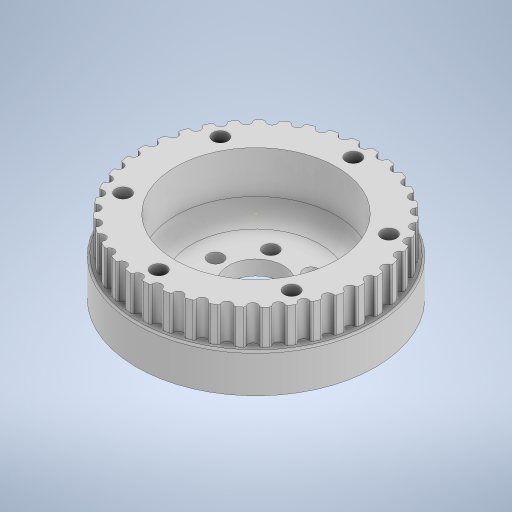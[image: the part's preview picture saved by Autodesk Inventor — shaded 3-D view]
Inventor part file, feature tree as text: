
AUTODESK INVENTOR PART (.ipt)
format: ipt  version: 2024 (Build 280153000, 153)  size: 675,328 bytes
history: native  units: mm
features: sketch x11, extrude x10, projected_geometry x4, fillet x3, pattern_circular x1
ambient origin geometry x8: Origin, YZ Plane, XZ Plane, XY Plane, X Axis, Y Axis, Z Axis, Center Point
bodies: Solid1 (feature_tree)
feature tree (29):
  extrude  "Extrusion1"  Depth=106.0mm
  extrude  "Extrusion2"  Depth=8.0mm TaperAngle=0.0deg
  extrude  "Extrusion3"  Depth=8.0mm TaperAngle=0.0deg
  extrude  "Extrusion4"  Depth=8.1mm
  extrude  "Extrusion5"  Depth=60.0mm
  extrude  "Extrusion6"  Depth=20.0mm TaperAngle=0.0deg
  extrude  "Extrusion7"  Depth=93.5mm
  extrude  "Extrusion8"  Depth=22.0mm TaperAngle=0.0deg
  extrude  "Extrusion9"  Depth=32.0mm TaperAngle=0.0deg
  pattern_circular  "Circular Pattern1"  Count=39 Angle=360.0deg
  fillet  "Fillet1"  Radius=9.0mm
  extrude  "Extrusion10"  Depth=1.0mm
  fillet  "Fillet2"  Radius=130.0mm
  sketch  "Sketch11"  dims[d39=5.1mm d40=125.0mm d41=130.0mm d42=21.0mm d43=0.0mm d44=61.9mm d45=1.0mm d46=1.0mm]
  fillet  "Fillet3"  Radius=21.0mm
  sketch  "Sketch1"  dims[d0=125.0mm d1=106.0mm]
  sketch  "Sketch2"  dims[d2=60.0mm d4=360.0deg d6=8.0mm d7=0.0mm]
  sketch  "Sketch3"  dims[d8=30.0mm d9=8.0mm d10=0.0mm]
  projected_geometry  "Projected Loop1"
  sketch  "Sketch4"  dims[d11=22.0mm d12=8.1mm]
  projected_geometry  "Projected Loop2"
  sketch  "Sketch5"  dims[d13=60.0mm d15=360.0deg d17=60.0mm]
  projected_geometry  "Projected Loop3"
  sketch  "Sketch6"  dims[d18=8.1mm d19=20.0mm d20=0.0mm]
  sketch  "Sketch7"  dims[d22=7.0mm d23=0.0mm d24=93.5mm]
  projected_geometry  "Projected Loop4"
  sketch  "Sketch8"  dims[d25=2.0mm d26=0.0mm d27=22.0mm d28=0.0mm]
  sketch  "Sketch9"  dims[d29=32.0mm d30=0.0mm d31=32.0mm d32=0.0mm]
  sketch  "Sketch10"  dims[d33=19.0mm d34=0.0mm d35=390.0mm d36=360.0deg d38=9.0mm]
